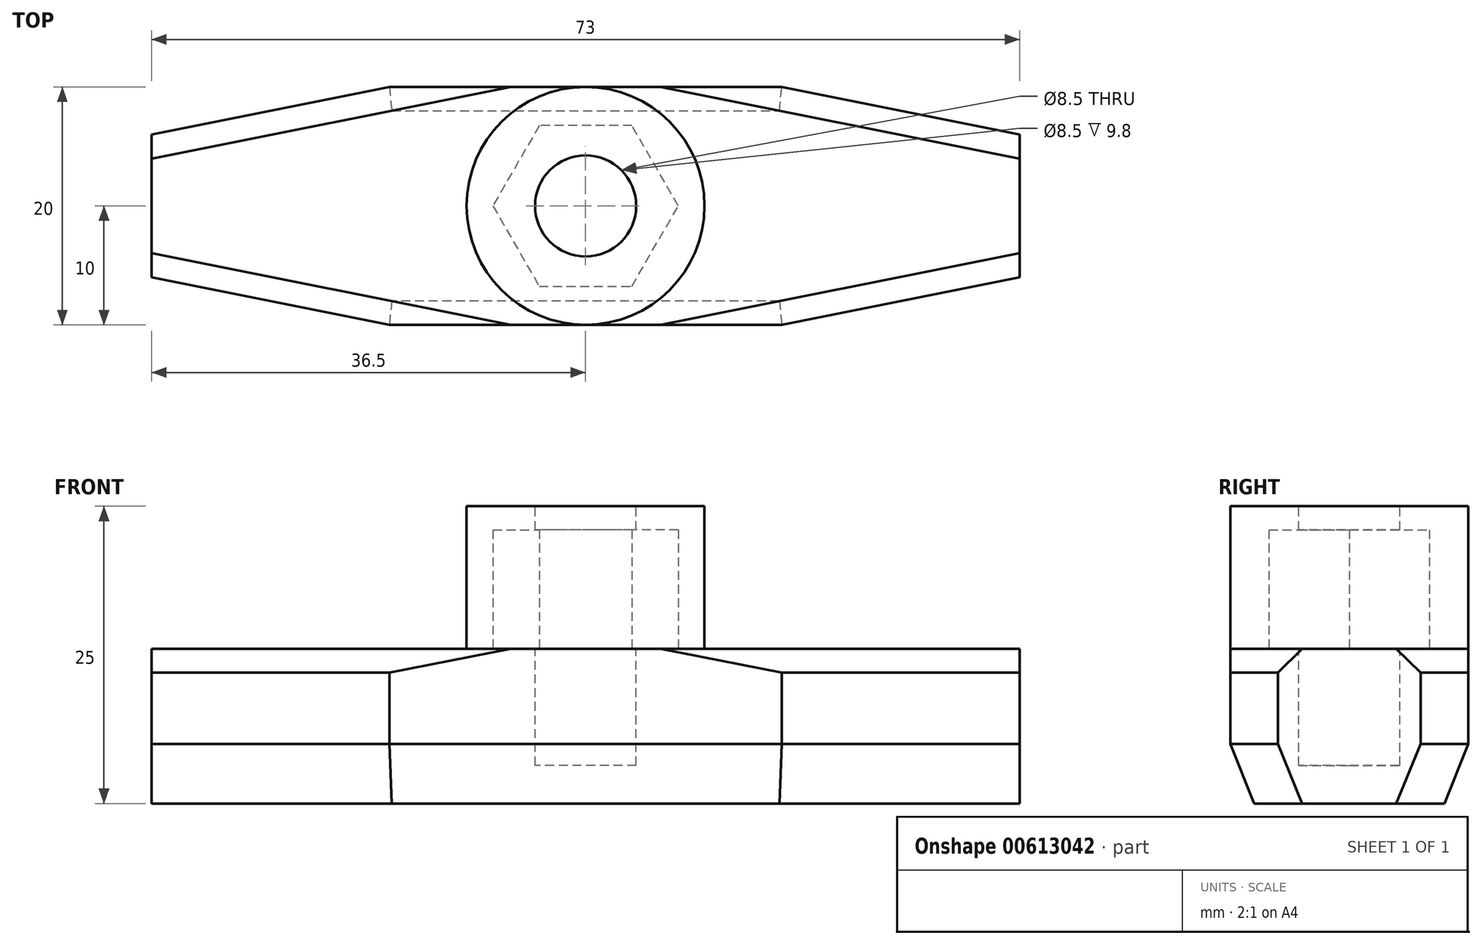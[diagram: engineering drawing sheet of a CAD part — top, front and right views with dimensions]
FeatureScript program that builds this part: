
annotation { "Feature Type Name" : "Feature", "Feature Type Description" : "" }
export const myFeature = defineFeature(function(context is Context, id is Id, definition is map)
    precondition{}
    {
        {
            var Q0;
            Q0=qCreatedBy(makeId("Top.planeOp"),FACE);
            var sketch = newSketch(context, id + "F0", { "sketchPlane" : qUnion([Q0])});
            skLineSegment(sketch, "E0.bottom", {"start": v(16.5, -10) * mm, "end": v(-16.5, -10) * mm});
            skLineSegment(sketch, "E0.top", {"start": v(16.5, 10) * mm, "end": v(-16.5, 10) * mm});
            skPoint(sketch, "E0.middle", {"position": v(0, 0) * mm});
            skLineSegment(sketch, "E1", {"start": v(-16.5, 10) * mm, "end": v(-36.5, 6) * mm});
            skLineSegment(sketch, "E2", {"start": v(-36.5, 6) * mm, "end": v(-36.5, -6) * mm});
            skLineSegment(sketch, "E3", {"start": v(-36.5, -6) * mm, "end": v(-16.5, -10) * mm});
            skLineSegment(sketch, "E4", {"start": v(16.5, -10) * mm, "end": v(36.5, -6) * mm});
            skLineSegment(sketch, "E5", {"start": v(36.5, -6) * mm, "end": v(36.5, 6) * mm});
            skLineSegment(sketch, "E6", {"start": v(36.5, 6) * mm, "end": v(16.5, 10) * mm});
            skSolve(sketch);
        }
        {
            var Q0;
            Q0=makeQuery(id+"F0.imprint","IMPRINT",FACE,{"disambiguationData":[TD([[makeQuery(id+"F0.imprint","IMPRINT",EDGE,{"derivedFrom":sQuery(id+"F0.wireOp",EDGE,"E0.bottom")}),-1.0]])]});
            extrude(context, id + "F1", {"entities" : qUnion([Q0]), "depth" : 13 * mm, "offsetDistance" : 25 * mm});
        }
        {
            var Q0;
            Q0=makeQuery(id+"F1.opExtrude","CAP_FACE",FACE,{"disambiguationData":[OSD([sQuery(id+"F0.wireOp",EDGE,"E0.bottom"),sQuery(id+"F0.wireOp",EDGE,"E0.top"),sQuery(id+"F0.wireOp",EDGE,"E1"),sQuery(id+"F0.wireOp",EDGE,"E2"),sQuery(id+"F0.wireOp",EDGE,"E3"),sQuery(id+"F0.wireOp",EDGE,"E4"),sQuery(id+"F0.wireOp",EDGE,"E5"),sQuery(id+"F0.wireOp",EDGE,"E6")])],"isStart":false});
            var sketch = newSketch(context, id + "F2", { "sketchPlane" : qUnion([Q0])});
            skCircle(sketch, "E7.cCircle", {"center": v(0, 0) * mm, "radius": 6.5 * mm, "construction": true});
            skLineSegment(sketch, "E7.0", {"start": v(3.75, -6.5) * mm, "end": v(-3.75, -6.5) * mm});
            skLineSegment(sketch, "E7.1", {"start": v(-3.75, -6.5) * mm, "end": v(-7.5, 0) * mm});
            skLineSegment(sketch, "E7.2", {"start": v(-7.5, 0) * mm, "end": v(-3.75, 6.5) * mm});
            skLineSegment(sketch, "E7.3", {"start": v(-3.75, 6.5) * mm, "end": v(3.75, 6.5) * mm});
            skLineSegment(sketch, "E7.4", {"start": v(3.75, 6.5) * mm, "end": v(7.5, 0) * mm});
            skLineSegment(sketch, "E7.5", {"start": v(7.5, 0) * mm, "end": v(3.75, -6.5) * mm});
            skPoint(sketch, "E7.0.midPoint", {"position": v(0, -6.5) * mm});
            skSolve(sketch);
        }
        {
            var Q0;
            Q0=makeQuery(id+"F2.imprint","IMPRINT",FACE,{"disambiguationData":[TD([[makeQuery(id+"F2.imprint","IMPRINT",EDGE,{"derivedFrom":sQuery(id+"F2.wireOp",EDGE,"E7.0")}),-1.0]])]});
            extrude(context, id + "F3", {"entities" : qUnion([Q0]), "operationType" : NewBodyOperationType.ADD, "depth" : 3.2 * mm, "offsetDistance" : 25 * mm});
        }
        {
            var Q0;
            Q0=makeQuery(id+"F3.opExtrude","CAP_FACE",FACE,{"disambiguationData":[OSD([sQuery(id+"F2.wireOp",EDGE,"E7.0"),sQuery(id+"F2.wireOp",EDGE,"E7.1"),sQuery(id+"F2.wireOp",EDGE,"E7.2"),sQuery(id+"F2.wireOp",EDGE,"E7.3"),sQuery(id+"F2.wireOp",EDGE,"E7.4"),sQuery(id+"F2.wireOp",EDGE,"E7.5")])],"isStart":false});
            var sketch = newSketch(context, id + "F4", { "sketchPlane" : qUnion([Q0])});
            skCircle(sketch, "E8", {"center": v(0, 0) * mm, "radius": 4.25 * mm});
            skSolve(sketch);
        }
        {
            var Q0;
            Q0=makeQuery(id+"F4.imprint","IMPRINT",FACE,{"disambiguationData":[TD([[makeQuery(id+"F4.imprint","IMPRINT",EDGE,{"derivedFrom":sQuery(id+"F4.wireOp",EDGE,"E8")}),1.0]])]});
            extrude(context, id + "F5", {"entities" : qUnion([Q0]), "operationType" : NewBodyOperationType.REMOVE, "oppositeDirection" : true, "depth" : 13 * mm, "offsetDistance" : 25 * mm});
        }
        {
            var Q0;
            Q0=makeQuery(id+"F1.opExtrude","CAP_EDGE",EDGE,{"disambiguationData":[OSD([sQuery(id+"F0.wireOp",EDGE,"E6")])],"isStart":true});
            var Q1;
            Q1=makeQuery(id+"F1.opExtrude","CAP_EDGE",EDGE,{"disambiguationData":[OSD([sQuery(id+"F0.wireOp",EDGE,"E4")])],"isStart":true});
            var Q2;
            Q2=makeQuery(id+"F1.opExtrude","CAP_EDGE",EDGE,{"disambiguationData":[OSD([sQuery(id+"F0.wireOp",EDGE,"E0.bottom")])],"isStart":true});
            var Q3;
            Q3=makeQuery(id+"F1.opExtrude","CAP_EDGE",EDGE,{"disambiguationData":[OSD([sQuery(id+"F0.wireOp",EDGE,"E3")])],"isStart":true});
            var Q4;
            Q4=makeQuery(id+"F1.opExtrude","CAP_EDGE",EDGE,{"disambiguationData":[OSD([sQuery(id+"F0.wireOp",EDGE,"E1")])],"isStart":true});
            var Q5;
            Q5=makeQuery(id+"F1.opExtrude","CAP_EDGE",EDGE,{"disambiguationData":[OSD([sQuery(id+"F0.wireOp",EDGE,"E0.top")])],"isStart":true});
            chamfer(context, id + "F6", {"entities" : qUnion([Q0, Q1, Q2, Q3, Q4, Q5]), "chamferType" : ChamferType.TWO_OFFSETS, "width1" : 5 * mm, "oppositeDirection" : false, "width2" : 2 * mm, "tangentPropagation" : true});
        }
        {
            var Q0;
            Q0=makeQuery(id+"F1.opExtrude","CAP_EDGE",EDGE,{"disambiguationData":[OSD([sQuery(id+"F0.wireOp",EDGE,"E4")])],"isStart":false});
            var Q1;
            Q1=makeQuery(id+"F1.opExtrude","CAP_EDGE",EDGE,{"disambiguationData":[OSD([sQuery(id+"F0.wireOp",EDGE,"E6")])],"isStart":false});
            var Q2;
            Q2=makeQuery(id+"F1.opExtrude","CAP_EDGE",EDGE,{"disambiguationData":[OSD([sQuery(id+"F0.wireOp",EDGE,"E1")])],"isStart":false});
            var Q3;
            Q3=makeQuery(id+"F1.opExtrude","CAP_EDGE",EDGE,{"disambiguationData":[OSD([sQuery(id+"F0.wireOp",EDGE,"E3")])],"isStart":false});
            chamfer(context, id + "F7", {"entities" : qUnion([Q0, Q1, Q2, Q3]), "width" : 2 * mm, "tangentPropagation" : true});
        }
        {
            var Q0;
            Q0=qCreatedBy(makeId("Top.planeOp"),FACE);
            cPlane(context, id + "F8", {"entities" : qUnion([Q0]), "cplaneType" : CPlaneType.OFFSET, "offset" : 25 * mm, "width" : 150 * mm, "height" : 150 * mm});
        }
        {
            var Q0;
            Q0=qCreatedBy(id+"F8.planeOp",FACE);
            var sketch = newSketch(context, id + "F9", { "sketchPlane" : qUnion([Q0])});
            skCircle(sketch, "E9", {"center": v(0, 0) * mm, "radius": 10 * mm});
            skCircle(sketch, "E10", {"center": v(0, 0) * mm, "radius": 4.25 * mm});
            skSolve(sketch);
        }
        {
            var Q0;
            Q0=makeQuery(id+"F9.imprint","IMPRINT",FACE,{"disambiguationData":[TD([[makeQuery(id+"F9.imprint","IMPRINT",EDGE,{"derivedFrom":sQuery(id+"F9.wireOp",EDGE,"E9")}),1.0]])]});
            extrude(context, id + "F10", {"entities" : qUnion([Q0]), "oppositeDirection" : true, "depth" : 12 * mm, "offsetDistance" : 25 * mm});
        }
        {
            var Q0;
            Q0=makeQuery(id+"F10.opExtrude","CAP_FACE",FACE,{"disambiguationData":[OSD([sQuery(id+"F9.wireOp",EDGE,"E9"),sQuery(id+"F9.wireOp",EDGE,"E10")])],"isStart":false});
            var sketch = newSketch(context, id + "F11", { "sketchPlane" : qUnion([Q0])});
            skCircle(sketch, "E11.cCircle", {"center": v(0, 0) * mm, "radius": 6.75 * mm, "construction": true});
            skLineSegment(sketch, "E11.0", {"start": v(3.9, -6.75) * mm, "end": v(-3.9, -6.75) * mm});
            skLineSegment(sketch, "E11.1", {"start": v(-3.9, -6.75) * mm, "end": v(-7.8, 0) * mm});
            skLineSegment(sketch, "E11.2", {"start": v(-7.8, 0) * mm, "end": v(-3.9, 6.75) * mm});
            skLineSegment(sketch, "E11.3", {"start": v(-3.9, 6.75) * mm, "end": v(3.9, 6.75) * mm});
            skLineSegment(sketch, "E11.4", {"start": v(3.9, 6.75) * mm, "end": v(7.8, 0) * mm});
            skLineSegment(sketch, "E11.5", {"start": v(7.8, 0) * mm, "end": v(3.9, -6.75) * mm});
            skPoint(sketch, "E11.0.midPoint", {"position": v(0, -6.75) * mm});
            skSolve(sketch);
        }
        {
            var Q0;
            Q0=makeQuery(id+"F11.imprint","IMPRINT",FACE,{"disambiguationData":[TD([[makeQuery(id+"F11.imprint","IMPRINT",EDGE,{"derivedFrom":sQuery(id+"F11.wireOp",EDGE,"E11.0")}),-1.0]])]});
            extrude(context, id + "F12", {"entities" : qUnion([Q0]), "operationType" : NewBodyOperationType.REMOVE, "oppositeDirection" : true, "depth" : 10 * mm, "offsetDistance" : 25 * mm});
        }
    });
